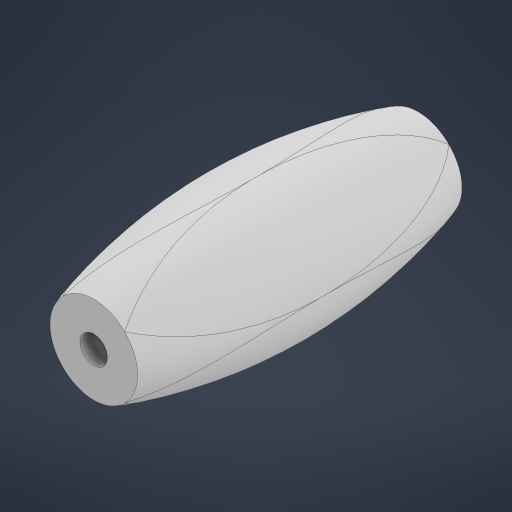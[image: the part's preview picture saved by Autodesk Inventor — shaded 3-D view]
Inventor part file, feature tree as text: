
AUTODESK INVENTOR PART (.ipt)
format: ipt  version: 2023 (Build 270158000, 158)  size: 437,248 bytes
history: native  units: mm
features: extrude x4, sketch x3, fillet x2
ambient origin geometry x8: Origin, YZ Plane, XZ Plane, XY Plane, X Axis, Y Axis, Z Axis, Center Point
bodies: Solid1 (feature_tree)
feature tree (9):
  extrude  "Extrusion1"  Depth=15.0mm
  sketch  "Sketch2"  dims[d2=3.0mm d3=35.56mm d4=0.0mm]
  sketch  "Sketch3"  dims[d5=2.0mm d6=2.0mm d7=2.0mm d8=2.0mm d9=35.56mm d10=0.0mm d11=35.56mm d12=0.0mm d13=35.56mm d14=0.0mm d15=7.499mm d16=5.0mm]
  extrude  "Extrusion2"  Depth=35.56mm TaperAngle=0.0deg
  extrude  "Extrusion3"  Depth=2.0mm
  extrude  "Extrusion4"  Depth=2.0mm
  fillet  "Fillet1"  Radius=2.0mm
  fillet  "Fillet2"  Radius=35.56mm
  sketch  "Sketch1"  dims[d0=15.0mm d1=15.0mm]
